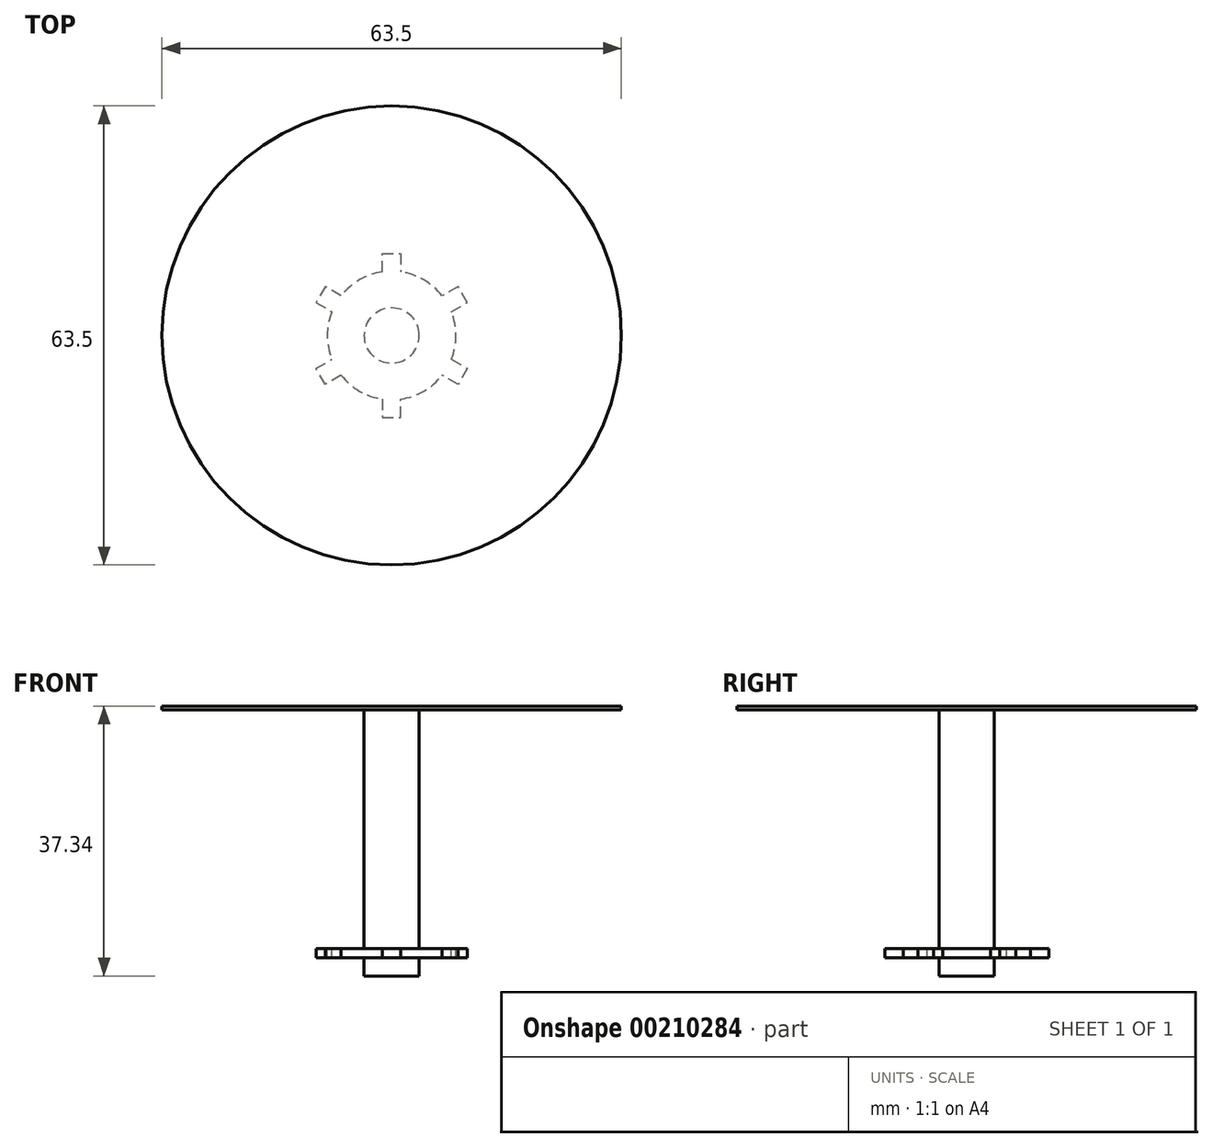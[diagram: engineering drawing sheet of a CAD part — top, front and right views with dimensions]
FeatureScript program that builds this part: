
annotation { "Feature Type Name" : "Feature", "Feature Type Description" : "" }
export const myFeature = defineFeature(function(context is Context, id is Id, definition is map)
    precondition{}
    {
        {
            var Q0;
            Q0=qCreatedBy(makeId("Top.planeOp"),FACE);
            var sketch = newSketch(context, id + "F0", { "sketchPlane" : qUnion([Q0])});
            skCircle(sketch, "E0", {"center": v(0, 0) * mm, "radius": 31.75 * mm});
            skSolve(sketch);
        }
        {
            var Q0;
            Q0=makeQuery(id+"F0.imprint","IMPRINT",FACE,{"disambiguationData":[TD([[makeQuery(id+"F0.imprint","IMPRINT",EDGE,{"derivedFrom":sQuery(id+"F0.wireOp",EDGE,"E0")}),1.0]])]});
            extrude(context, id + "F1", {"entities" : qUnion([Q0]), "depth" : 0.5 * mm});
        }
        {
            var Q0;
            Q0=makeQuery(id+"F1.opExtrude","CAP_FACE",FACE,{"disambiguationData":[OSD([sQuery(id+"F0.wireOp",EDGE,"E0")])],"isStart":true});
            var sketch = newSketch(context, id + "F2", { "sketchPlane" : qUnion([Q0])});
            skCircle(sketch, "E1", {"center": v(0, 0) * mm, "radius": 3.8 * mm});
            skSolve(sketch);
        }
        {
            var Q0;
            Q0=makeQuery(id+"F2.imprint","IMPRINT",FACE,{"disambiguationData":[TD([[makeQuery(id+"F2.imprint","IMPRINT",EDGE,{"derivedFrom":sQuery(id+"F2.wireOp",EDGE,"E1")}),1.0]])]});
            extrude(context, id + "F3", {"entities" : qUnion([Q0]), "operationType" : NewBodyOperationType.ADD, "depth" : 33.02 * mm});
        }
        {
            var Q0;
            Q0=makeQuery(id+"F3.opExtrude","CAP_FACE",FACE,{"disambiguationData":[OSD([sQuery(id+"F2.wireOp",EDGE,"E1")])],"isStart":false});
            var sketch = newSketch(context, id + "F4", { "sketchPlane" : qUnion([Q0])});
            skCircle(sketch, "E2", {"center": v(0, 0) * mm, "radius": 8.9 * mm});
            skLineSegment(sketch, "E3", {"start": v(-1.27, 8.8) * mm, "end": v(-1.27, 11.34) * mm});
            skLineSegment(sketch, "E4", {"start": v(-1.27, 11.34) * mm, "end": v(1.27, 11.34) * mm});
            skLineSegment(sketch, "E5", {"start": v(1.27, 11.34) * mm, "end": v(1.27, 8.8) * mm});
            skLineSegment(sketch, "E6", {"start": v(-1.27, -8.8) * mm, "end": v(-1.27, -11.34) * mm});
            skLineSegment(sketch, "E7", {"start": v(-1.27, -11.34) * mm, "end": v(1.27, -11.34) * mm});
            skLineSegment(sketch, "E8", {"start": v(1.27, -11.34) * mm, "end": v(1.27, -8.8) * mm});
            skLineSegment(sketch, "E9.1.0", {"start": v(-6.98, -5.5) * mm, "end": v(-9.18, -6.77) * mm});
            skLineSegment(sketch, "E9.1.1", {"start": v(-9.18, -6.77) * mm, "end": v(-10.45, -4.57) * mm});
            skLineSegment(sketch, "E9.1.2", {"start": v(-10.45, -4.57) * mm, "end": v(-8.26, -3.3) * mm});
            skLineSegment(sketch, "E9.2.0", {"start": v(8.25, -3.3) * mm, "end": v(10.45, -4.57) * mm});
            skLineSegment(sketch, "E9.2.1", {"start": v(10.45, -4.57) * mm, "end": v(9.18, -6.77) * mm});
            skLineSegment(sketch, "E9.2.2", {"start": v(9.18, -6.77) * mm, "end": v(6.98, -5.5) * mm});
            skLineSegment(sketch, "E10.1.0", {"start": v(8.26, 3.3) * mm, "end": v(10.45, 4.57) * mm});
            skLineSegment(sketch, "E10.1.1", {"start": v(9.18, 6.77) * mm, "end": v(6.99, 5.5) * mm});
            skLineSegment(sketch, "E10.1.2", {"start": v(10.45, 4.57) * mm, "end": v(9.18, 6.77) * mm});
            skLineSegment(sketch, "E10.2.0", {"start": v(-6.98, 5.5) * mm, "end": v(-9.18, 6.77) * mm});
            skLineSegment(sketch, "E10.2.1", {"start": v(-10.45, 4.57) * mm, "end": v(-8.25, 3.3) * mm});
            skLineSegment(sketch, "E10.2.2", {"start": v(-9.18, 6.77) * mm, "end": v(-10.45, 4.57) * mm});
            skSolve(sketch);
        }
        {
            var Q0;
            Q0=makeQuery(id+"F4.imprint","IMPRINT",FACE,{"disambiguationData":[TD([[makeQuery(id+"F4.imprint","IMPRINT",EDGE,{"derivedFrom":makeQuery(id+"F3.opExtrude","CAP_EDGE",EDGE,{"disambiguationData":[OSD([sQuery(id+"F2.wireOp",EDGE,"E1")])],"isStart":false})}),-1.0]])]});
            var Q1;
            Q1=makeQuery(id+"F4.imprint","IMPRINT",FACE,{"disambiguationData":[TD([[makeQuery(id+"F4.imprint","IMPRINT",EDGE,{"derivedFrom":makeQuery(id+"F3.opExtrude","CAP_EDGE",EDGE,{"disambiguationData":[OSD([sQuery(id+"F2.wireOp",EDGE,"E1")])],"isStart":false})}),1.0]])]});
            var Q2;
            {var subQ0=sQuery(id+"F4.wireOp",EDGE,"E3");Q2=makeQuery(id+"F4.imprint","IMPRINT",FACE,{"disambiguationData":[TD([[makeQuery(id+"F4.imprint","IMPRINT",EDGE,{"derivedFrom":subQ0}),-1.0]])]});}
            var Q3;
            {var subQ0=sQuery(id+"F4.wireOp",EDGE,"E10.1.0");Q3=makeQuery(id+"F4.imprint","IMPRINT",FACE,{"disambiguationData":[TD([[makeQuery(id+"F4.imprint","IMPRINT",EDGE,{"derivedFrom":subQ0}),1.0]])]});}
            var Q4;
            {var subQ0=sQuery(id+"F4.wireOp",EDGE,"E9.2.0");Q4=makeQuery(id+"F4.imprint","IMPRINT",FACE,{"disambiguationData":[TD([[makeQuery(id+"F4.imprint","IMPRINT",EDGE,{"derivedFrom":subQ0}),-1.0]])]});}
            var Q5;
            {var subQ0=sQuery(id+"F4.wireOp",EDGE,"E6");Q5=makeQuery(id+"F4.imprint","IMPRINT",FACE,{"disambiguationData":[TD([[makeQuery(id+"F4.imprint","IMPRINT",EDGE,{"derivedFrom":subQ0}),1.0]])]});}
            var Q6;
            {var subQ0=sQuery(id+"F4.wireOp",EDGE,"E9.1.0");Q6=makeQuery(id+"F4.imprint","IMPRINT",FACE,{"disambiguationData":[TD([[makeQuery(id+"F4.imprint","IMPRINT",EDGE,{"derivedFrom":subQ0}),-1.0]])]});}
            var Q7;
            {var subQ0=sQuery(id+"F4.wireOp",EDGE,"E10.2.0");Q7=makeQuery(id+"F4.imprint","IMPRINT",FACE,{"disambiguationData":[TD([[makeQuery(id+"F4.imprint","IMPRINT",EDGE,{"derivedFrom":subQ0}),1.0]])]});}
            extrude(context, id + "F5", {"entities" : qUnion([Q0, Q1, Q2, Q3, Q4, Q5, Q6, Q7]), "operationType" : NewBodyOperationType.ADD, "depth" : 1.27 * mm});
        }
        {
            var Q0;
            Q0=makeQuery(id+"F5.opExtrude","CAP_FACE",FACE,{"disambiguationData":[OSD([sQuery(id+"F4.wireOp",EDGE,"E2"),sQuery(id+"F4.wireOp",EDGE,"E3"),sQuery(id+"F4.wireOp",EDGE,"E4"),sQuery(id+"F4.wireOp",EDGE,"E5"),sQuery(id+"F4.wireOp",EDGE,"E6"),sQuery(id+"F4.wireOp",EDGE,"E7"),sQuery(id+"F4.wireOp",EDGE,"E8"),sQuery(id+"F4.wireOp",EDGE,"E9.1.0"),sQuery(id+"F4.wireOp",EDGE,"E9.1.1"),sQuery(id+"F4.wireOp",EDGE,"E9.1.2"),sQuery(id+"F4.wireOp",EDGE,"E9.2.0"),sQuery(id+"F4.wireOp",EDGE,"E9.2.1"),sQuery(id+"F4.wireOp",EDGE,"E9.2.2"),sQuery(id+"F4.wireOp",EDGE,"E10.1.0"),sQuery(id+"F4.wireOp",EDGE,"E10.1.1"),sQuery(id+"F4.wireOp",EDGE,"E10.1.2"),sQuery(id+"F4.wireOp",EDGE,"E10.2.0"),sQuery(id+"F4.wireOp",EDGE,"E10.2.1"),sQuery(id+"F4.wireOp",EDGE,"E10.2.2")])],"isStart":false});
            var sketch = newSketch(context, id + "F6", { "sketchPlane" : qUnion([Q0])});
            skCircle(sketch, "E11", {"center": v(0, 0) * mm, "radius": 3.81 * mm});
            skSolve(sketch);
        }
        {
            var Q0;
            Q0=makeQuery(id+"F6.imprint","IMPRINT",FACE,{"disambiguationData":[TD([[makeQuery(id+"F6.imprint","IMPRINT",EDGE,{"derivedFrom":sQuery(id+"F6.wireOp",EDGE,"E11")}),1.0]])]});
            extrude(context, id + "F7", {"entities" : qUnion([Q0]), "operationType" : NewBodyOperationType.ADD, "depth" : 2.54 * mm});
        }
    });
